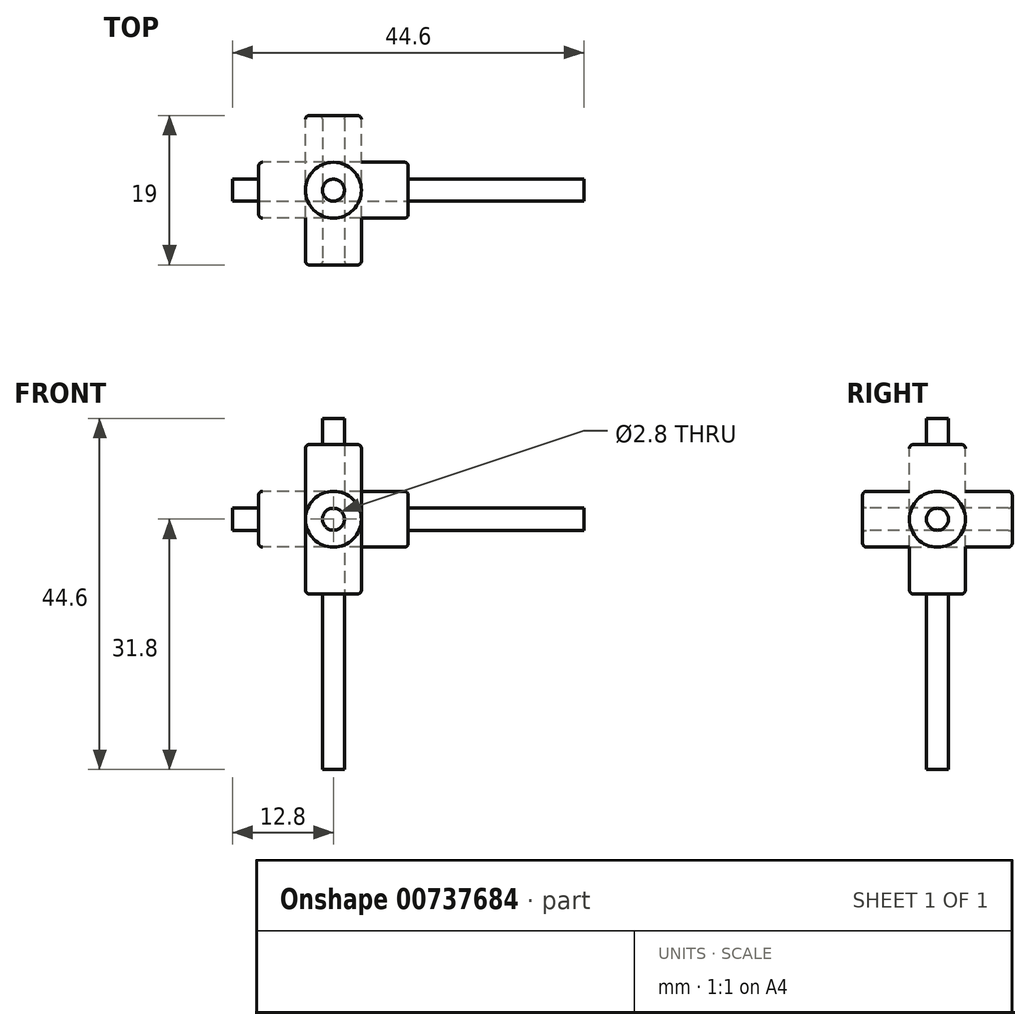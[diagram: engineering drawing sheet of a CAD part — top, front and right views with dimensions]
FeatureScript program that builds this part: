
annotation { "Feature Type Name" : "Feature", "Feature Type Description" : "" }
export const myFeature = defineFeature(function(context is Context, id is Id, definition is map)
    precondition{}
    {
        {
            var Q0;
            Q0=qCreatedBy(makeId("Front.planeOp"),FACE);
            var sketch = newSketch(context, id + "F0", { "sketchPlane" : qUnion([Q0])});
            skCircle(sketch, "E0", {"center": v(0, 0) * mm, "radius": 3.55 * mm});
            skSolve(sketch);
        }
        {
            var Q0;
            Q0=makeQuery(id+"F0.imprint","IMPRINT",FACE,{"disambiguationData":[TD([[makeQuery(id+"F0.imprint","IMPRINT",EDGE,{"derivedFrom":sQuery(id+"F0.wireOp",EDGE,"E0")}),1.0]])]});
            extrude(context, id + "F1", {"entities" : qUnion([Q0]), "endBound" : BoundingType.SYMMETRIC, "depth" : 19 * mm, "offsetDistance" : 25 * mm});
        }
        {
            var Q0;
            Q0=qCreatedBy(makeId("Front.planeOp"),FACE);
            var sketch = newSketch(context, id + "F2", { "sketchPlane" : qUnion([Q0])});
            skLineSegment(sketch, "E1.bottom", {"start": v(0, 0) * mm, "end": v(-10, 0) * mm});
            skLineSegment(sketch, "E1.top", {"start": v(0, 10) * mm, "end": v(-10, 10) * mm});
            skLineSegment(sketch, "E1.left", {"start": v(0, 0) * mm, "end": v(0, 10) * mm});
            skLineSegment(sketch, "E1.right", {"start": v(-10, 0) * mm, "end": v(-10, 10) * mm});
            skSolve(sketch);
        }
        {
            var Q0;
            Q0=makeQuery(id+"F2.imprint","IMPRINT",FACE,{"disambiguationData":[TD([[makeQuery(id+"F2.imprint","IMPRINT",EDGE,{"derivedFrom":sQuery(id+"F2.wireOp",EDGE,"E1.bottom")}),-1.0]])]});
            extrude(context, id + "F3", {"entities" : qUnion([Q0]), "oppositeDirection" : true, "depth" : 10 * mm, "offsetDistance" : 25 * mm});
        }
        {
            var Q0;
            Q0=makeQuery(id+"F3.opExtrude","CAP_VERTEX",VERTEX,{"disambiguationData":[OSD([sQuery(id+"F2.wireOp",EDGE,"E1.top"),sQuery(id+"F2.wireOp",EDGE,"E1.left")])],"isStart":true});
            var Q1;
            Q1=makeQuery(id+"F3.opExtrude","CAP_VERTEX",VERTEX,{"disambiguationData":[OSD([sQuery(id+"F2.wireOp",EDGE,"E1.top"),sQuery(id+"F2.wireOp",EDGE,"E1.right")])],"isStart":false});
            var Q2;
            Q2=makeQuery(id+"F3.opExtrude","CAP_VERTEX",VERTEX,{"disambiguationData":[OSD([sQuery(id+"F2.wireOp",EDGE,"E1.bottom"),sQuery(id+"F2.wireOp",EDGE,"E1.right")])],"isStart":false});
            cPlane(context, id + "F4", {"entities" : qUnion([Q0, Q1, Q2]), "cplaneType" : CPlaneType.THREE_POINT, "offset" : 25 * mm, "width" : 150 * mm, "height" : 150 * mm});
        }
        {
            var Q0;
            Q0=qCreatedBy(id+"F4.planeOp",FACE);
            var sketch = newSketch(context, id + "F5", { "sketchPlane" : qUnion([Q0])});
            skLineSegment(sketch, "E2", {"start": v(0, 0) * mm, "end": v(14.14, 10) * mm});
            skSolve(sketch);
        }
        {
            var Q0;
            Q0=makeQuery(id+"F1.opExtrude","SWEPT_BODY",BODY,{"disambiguationData":[OSD([sQuery(id+"F0.wireOp",EDGE,"E0")])]});
            var Q1;
            Q1=sQuery(id+"F5.wireOp",EDGE,"E2");
            circularPattern(context, id + "F6", {"entities" : qUnion([Q0]), "axis" : qUnion([Q1]), "angle" : 360 * degree, "instanceCount" : 3, "equalSpace" : true});
        }
        {
            var Q0;
            Q0=makeQuery(id+"F3.opExtrude","SWEPT_BODY",BODY,{"disambiguationData":[OSD([sQuery(id+"F2.wireOp",EDGE,"E1.bottom"),sQuery(id+"F2.wireOp",EDGE,"E1.top"),sQuery(id+"F2.wireOp",EDGE,"E1.left"),sQuery(id+"F2.wireOp",EDGE,"E1.right")])]});
            deleteBodies(context, id + "F7", {"entities" : qUnion([Q0])});
        }
        {
            var Q0;
            Q0=makeQuery(id+"F1.opExtrude","CAP_FACE",FACE,{"disambiguationData":[OSD([sQuery(id+"F0.wireOp",EDGE,"E0")])],"isStart":false});
            var sketch = newSketch(context, id + "F8", { "sketchPlane" : qUnion([Q0])});
            skCircle(sketch, "E3", {"center": v(0, 0) * mm, "radius": 1.4 * mm});
            skSolve(sketch);
        }
        {
            var Q0;
            Q0=makeQuery(id+"F8.imprint","IMPRINT",FACE,{"disambiguationData":[TD([[makeQuery(id+"F8.imprint","IMPRINT",EDGE,{"derivedFrom":sQuery(id+"F8.wireOp",EDGE,"E3")}),1.0]])]});
            extrude(context, id + "F9", {"entities" : qUnion([Q0]), "endBound" : BoundingType.SYMMETRIC, "oppositeDirection" : true, "depth" : 44.6 * mm, "offsetDistance" : 25 * mm});
        }
        {
            var Q0;
            Q0=makeQuery(id+"F9.opExtrude","SWEPT_BODY",BODY,{"disambiguationData":[OSD([sQuery(id+"F8.wireOp",EDGE,"E3")])]});
            var Q1;
            Q1=sQuery(id+"F5.wireOp",EDGE,"E2");
            circularPattern(context, id + "F10", {"entities" : qUnion([Q0]), "axis" : qUnion([Q1]), "angle" : 360 * degree, "instanceCount" : 3, "equalSpace" : true});
        }
        {
            var Q0;
            Q0=makeQuery(id+"F9.opExtrude","SWEPT_BODY",BODY,{"disambiguationData":[OSD([sQuery(id+"F8.wireOp",EDGE,"E3")])]});
            var Q1;
            Q1=makeQuery(id+"F1.opExtrude","SWEPT_BODY",BODY,{"disambiguationData":[OSD([sQuery(id+"F0.wireOp",EDGE,"E0")])]});
            booleanBodies(context, id + "F11", {"operationType" : BooleanOperationType.SUBTRACTION, "tools" : qUnion([Q0]), "targets" : qUnion([Q1])});
        }
        {
            var Q0;
            Q0=makeQuery(id+"F6.opPattern","COPY",EDGE,{"derivedFrom":makeQuery(id+"F1.opExtrude","CAP_EDGE",EDGE,{"disambiguationData":[OSD([sQuery(id+"F0.wireOp",EDGE,"E0")])],"isStart":true}),"instanceName":"2"});
            var Q1;
            Q1=makeQuery(id+"F6.opPattern","COPY",FACE,{"derivedFrom":makeQuery(id+"F1.opExtrude","CAP_FACE",FACE,{"disambiguationData":[OSD([sQuery(id+"F0.wireOp",EDGE,"E0")])],"isStart":true}),"instanceName":"2"});
            var Q2;
            Q2=makeQuery(id+"F1.opExtrude","CAP_FACE",FACE,{"disambiguationData":[OSD([sQuery(id+"F0.wireOp",EDGE,"E0")])],"isStart":false});
            var Q3;
            Q3=makeQuery(id+"F6.opPattern","COPY",FACE,{"derivedFrom":makeQuery(id+"F1.opExtrude","CAP_FACE",FACE,{"disambiguationData":[OSD([sQuery(id+"F0.wireOp",EDGE,"E0")])],"isStart":false}),"instanceName":"2"});
            var Q4;
            Q4=makeQuery(id+"F1.opExtrude","CAP_FACE",FACE,{"disambiguationData":[OSD([sQuery(id+"F0.wireOp",EDGE,"E0")])],"isStart":true});
            var Q5;
            Q5=makeQuery(id+"F6.opPattern","COPY",FACE,{"derivedFrom":makeQuery(id+"F1.opExtrude","CAP_FACE",FACE,{"disambiguationData":[OSD([sQuery(id+"F0.wireOp",EDGE,"E0")])],"isStart":false}),"instanceName":"1"});
            var Q6;
            Q6=makeQuery(id+"F6.opPattern","COPY",FACE,{"derivedFrom":makeQuery(id+"F1.opExtrude","CAP_FACE",FACE,{"disambiguationData":[OSD([sQuery(id+"F0.wireOp",EDGE,"E0")])],"isStart":true}),"instanceName":"1"});
            fillet(context, id + "F12", {"entities" : qUnion([Q0, Q1, Q2, Q3, Q4, Q5, Q6]), "radius" : 0.5 * mm, "tangentPropagation" : true, "allowEdgeOverflow" : false});
        }
    });
